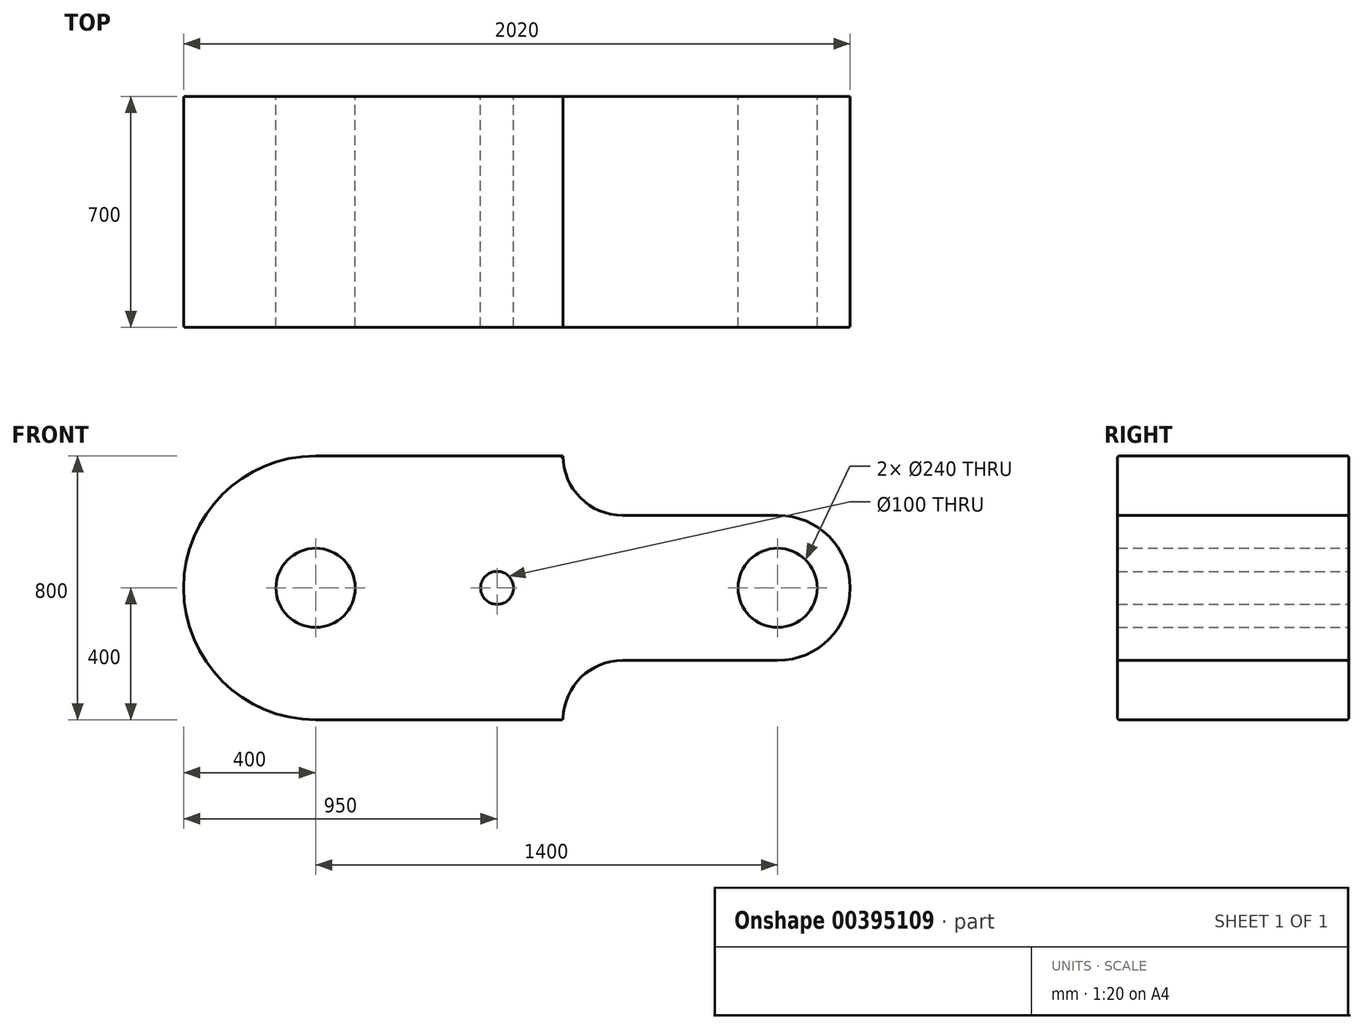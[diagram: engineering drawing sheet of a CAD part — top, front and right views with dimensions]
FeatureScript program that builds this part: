
annotation { "Feature Type Name" : "Feature", "Feature Type Description" : "" }
export const myFeature = defineFeature(function(context is Context, id is Id, definition is map)
    precondition{}
    {
        {
            var Q0;
            Q0=qCreatedBy(makeId("Front.planeOp"),FACE);
            var sketch = newSketch(context, id + "F0", { "sketchPlane" : qUnion([Q0])});
            skLineSegment(sketch, "E0.bottom", {"start": v(375, -400) * mm, "end": v(-375, -400) * mm});
            skLineSegment(sketch, "E0.top", {"start": v(375, 400) * mm, "end": v(-375, 400) * mm});
            skPoint(sketch, "E0.middle", {"position": v(0, 0) * mm});
            skArc(sketch, "E1", {"start": v(-375, 400) * mm, "mid": v(-775, 0) * mm, "end": v(-375, -400) * mm});
            skCircle(sketch, "E2", {"center": v(-375, 0) * mm, "radius": 120 * mm});
            skLineSegment(sketch, "E3.bottom", {"start": v(555, 220) * mm, "end": v(1025, 220) * mm});
            skLineSegment(sketch, "E3.top", {"start": v(555, -220) * mm, "end": v(1025, -220) * mm});
            skPoint(sketch, "E4", {"position": v(375, 0) * mm});
            skArc(sketch, "E5", {"start": v(555, -220) * mm, "mid": v(427.72, -272.72) * mm, "end": v(375, -400) * mm});
            skArc(sketch, "E6.MirrorCS", {"start": v(555, 220) * mm, "mid": v(427.72, 272.72) * mm, "end": v(375, 400) * mm});
            skPoint(sketch, "E7.orphan", {"position": v(375, -220) * mm});
            skPoint(sketch, "E0.left.end.orphan", {"position": v(375, 220) * mm});
            skCircle(sketch, "E8", {"center": v(175, 0) * mm, "radius": 50 * mm});
            skCircle(sketch, "E9", {"center": v(1025, 0) * mm, "radius": 120 * mm});
            skArc(sketch, "E10", {"start": v(1025, -220) * mm, "mid": v(1245, 0) * mm, "end": v(1025, 220) * mm});
            skSolve(sketch);
        }
        {
            var Q0;
            Q0=makeQuery(id+"F0.imprint","IMPRINT",FACE,{"disambiguationData":[TD([[makeQuery(id+"F0.imprint","IMPRINT",EDGE,{"derivedFrom":sQuery(id+"F0.wireOp",EDGE,"E0.bottom")}),-1.0]])]});
            extrude(context, id + "F1", {"entities" : qUnion([Q0]), "endBound" : BoundingType.SYMMETRIC, "depth" : 700 * mm});
        }
        {
            var Q0;
            Q0=makeQuery(id+"F1.opExtrude","CAP_EDGE",EDGE,{"disambiguationData":[OSD([sQuery(id+"F0.wireOp",EDGE,"E1")])],"isStart":false});
            var Q1;
            Q1=makeQuery(id+"F1.opExtrude","CAP_EDGE",EDGE,{"disambiguationData":[OSD([sQuery(id+"F0.wireOp",EDGE,"E0.top")])],"isStart":false});
            var Q2;
            Q2=makeQuery(id+"F1.opExtrude","CAP_EDGE",EDGE,{"disambiguationData":[OSD([sQuery(id+"F0.wireOp",EDGE,"E6.MirrorCS")])],"isStart":false});
            var Q3;
            Q3=makeQuery(id+"F1.opExtrude","CAP_EDGE",EDGE,{"disambiguationData":[OSD([sQuery(id+"F0.wireOp",EDGE,"E3.bottom")])],"isStart":false});
            var Q4;
            Q4=makeQuery(id+"F1.opExtrude","CAP_EDGE",EDGE,{"disambiguationData":[OSD([sQuery(id+"F0.wireOp",EDGE,"E10")])],"isStart":false});
            var Q5;
            Q5=makeQuery(id+"F1.opExtrude","CAP_EDGE",EDGE,{"disambiguationData":[OSD([sQuery(id+"F0.wireOp",EDGE,"E3.top")])],"isStart":false});
            var Q6;
            Q6=makeQuery(id+"F1.opExtrude","CAP_EDGE",EDGE,{"disambiguationData":[OSD([sQuery(id+"F0.wireOp",EDGE,"E5")])],"isStart":false});
            var Q7;
            Q7=makeQuery(id+"F1.opExtrude","CAP_EDGE",EDGE,{"disambiguationData":[OSD([sQuery(id+"F0.wireOp",EDGE,"E0.bottom")])],"isStart":false});
            var Q8;
            Q8=makeQuery(id+"F1.opExtrude","CAP_EDGE",EDGE,{"disambiguationData":[OSD([sQuery(id+"F0.wireOp",EDGE,"E1")])],"isStart":true});
            var Q9;
            Q9=makeQuery(id+"F1.opExtrude","CAP_EDGE",EDGE,{"disambiguationData":[OSD([sQuery(id+"F0.wireOp",EDGE,"E0.top")])],"isStart":true});
            var Q10;
            Q10=makeQuery(id+"F1.opExtrude","CAP_EDGE",EDGE,{"disambiguationData":[OSD([sQuery(id+"F0.wireOp",EDGE,"E6.MirrorCS")])],"isStart":true});
            var Q11;
            Q11=makeQuery(id+"F1.opExtrude","CAP_EDGE",EDGE,{"disambiguationData":[OSD([sQuery(id+"F0.wireOp",EDGE,"E3.bottom")])],"isStart":true});
            var Q12;
            Q12=makeQuery(id+"F1.opExtrude","CAP_EDGE",EDGE,{"disambiguationData":[OSD([sQuery(id+"F0.wireOp",EDGE,"E10")])],"isStart":true});
            var Q13;
            Q13=makeQuery(id+"F1.opExtrude","SWEPT_EDGE",EDGE,{"disambiguationData":[OSD([sQuery(id+"F0.wireOp",EDGE,"E0.bottom"),sQuery(id+"F0.wireOp",EDGE,"E5")])]});
            var Q14;
            Q14=makeQuery(id+"F1.opExtrude","CAP_EDGE",EDGE,{"disambiguationData":[OSD([sQuery(id+"F0.wireOp",EDGE,"E3.top")])],"isStart":true});
            var Q15;
            Q15=makeQuery(id+"F1.opExtrude","CAP_EDGE",EDGE,{"disambiguationData":[OSD([sQuery(id+"F0.wireOp",EDGE,"E5")])],"isStart":true});
            var Q16;
            Q16=makeQuery(id+"F1.opExtrude","CAP_EDGE",EDGE,{"disambiguationData":[OSD([sQuery(id+"F0.wireOp",EDGE,"E0.bottom")])],"isStart":true});
            fillet(context, id + "F2", {"entities" : qUnion([Q0, Q1, Q2, Q3, Q4, Q5, Q6, Q7, Q8, Q9, Q10, Q11, Q12, Q13, Q14, Q15, Q16]), "radius" : 5 * mm, "tangentPropagation" : true, "allowEdgeOverflow" : false});
        }
    });
